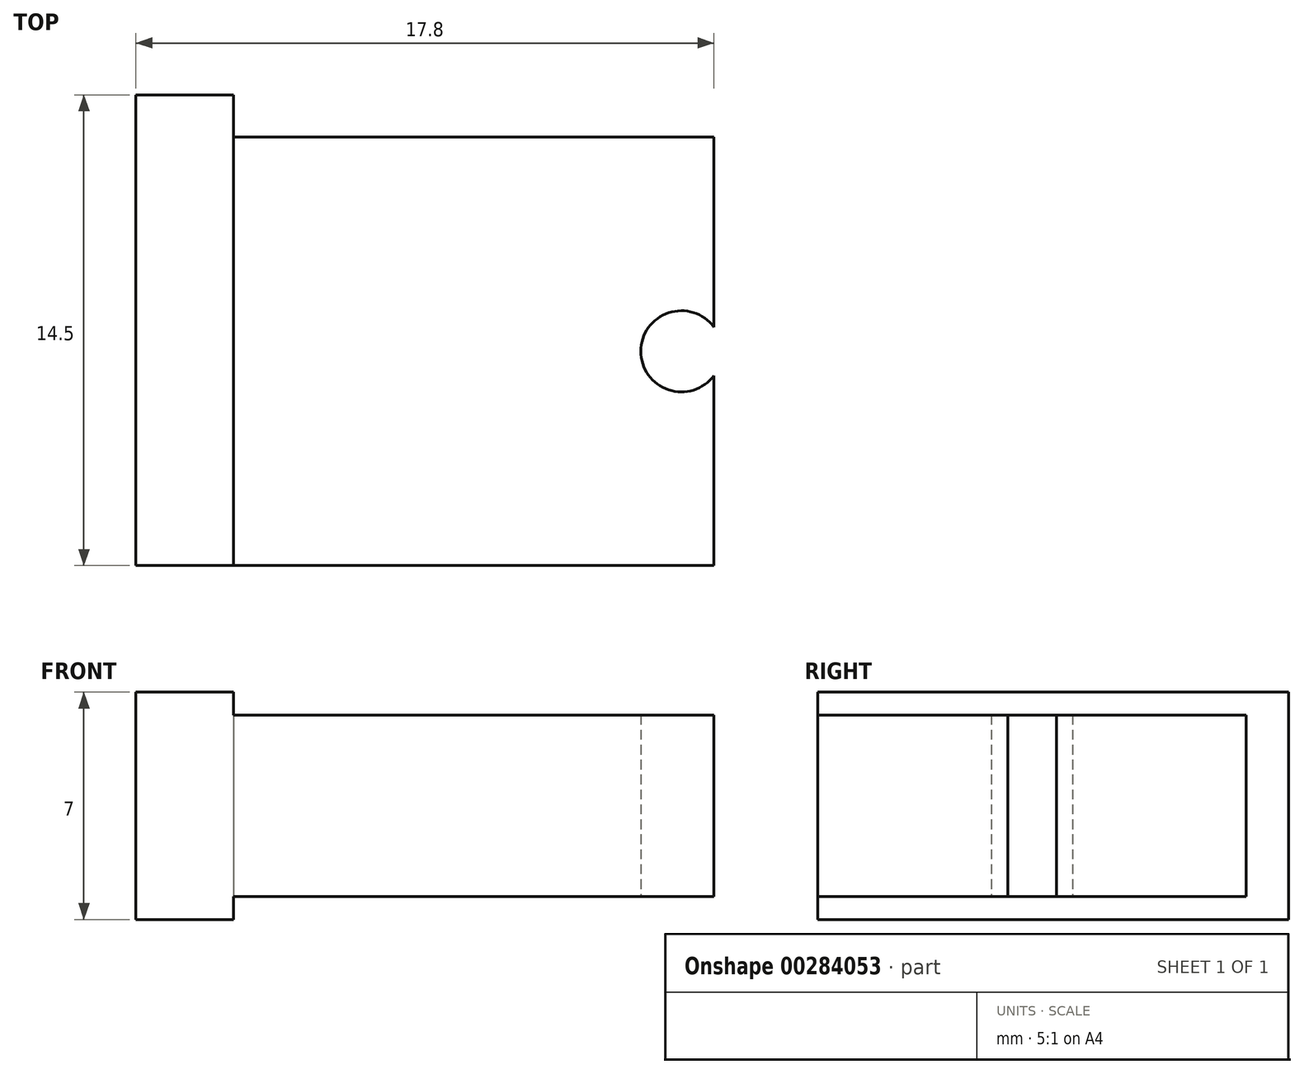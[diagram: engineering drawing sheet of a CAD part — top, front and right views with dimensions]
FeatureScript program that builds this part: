
annotation { "Feature Type Name" : "Feature", "Feature Type Description" : "" }
export const myFeature = defineFeature(function(context is Context, id is Id, definition is map)
    precondition{}
    {
        {
            var Q0;
            Q0=qCreatedBy(makeId("Top.planeOp"),FACE);
            var sketch = newSketch(context, id + "F0", { "sketchPlane" : qUnion([Q0])});
            skLineSegment(sketch, "E0.bottom", {"start": v(-7.4, 6.6) * mm, "end": v(7.4, 6.6) * mm});
            skLineSegment(sketch, "E0.top", {"start": v(-7.4, -6.6) * mm, "end": v(7.4, -6.6) * mm});
            skLineSegment(sketch, "E0.left", {"start": v(-7.4, 6.6) * mm, "end": v(-7.4, -6.6) * mm});
            skLineSegment(sketch, "E0.right", {"start": v(7.4, 6.6) * mm, "end": v(7.4, -6.6) * mm});
            skPoint(sketch, "E0.middle", {"position": v(0, 0) * mm});
            skLineSegment(sketch, "E1", {"start": v(-7.4, 0) * mm, "end": v(6.4, 0) * mm});
            skPoint(sketch, "E1.endSnap0", {"position": v(-7.4, 0) * mm});
            skCircle(sketch, "E2", {"center": v(6.4, 0) * mm, "radius": 1.1 * mm});
            skSolve(sketch);
        }
        {
            var Q0;
            Q0 = qSketchRegion(id + "F0", true);
            extrude(context, id + "F1", {"entities" : qUnion([Q0]), "depth" : 5.6 * mm});
        }
        {
            var Q0;
            Q0=sQuery(id+"F0.wireOp",VERTEX,"E2.center");
            var Q1;
            Q1=makeQuery(id+"F1.opExtrude","SWEPT_BODY",BODY,{"disambiguationData":[OSD([sQuery(id+"F0.wireOp",EDGE,"E0.bottom"),sQuery(id+"F0.wireOp",EDGE,"E0.top"),sQuery(id+"F0.wireOp",EDGE,"E0.left"),sQuery(id+"F0.wireOp",EDGE,"E0.right"),sQuery(id+"F0.wireOp",EDGE,"E2")])]});
            hole(context, id + "F2", {"style" : HoleStyle.SIMPLE, "endStyle" : HoleEndStyle.BLIND, "oppositeDirection" : true, "holeDiameter" : 2.5 * mm, "holeDepth" : 12 * mm, "tappedDepth" : 12 * mm, "tapClearance" : 3, "startFromSketch" : true, "locations" : qUnion([Q0]), "scope" : qUnion([Q1])});
        }
        {
            var Q0;
            Q0=makeQuery(id+"F1.opExtrude","SWEPT_FACE",FACE,{"disambiguationData":[OSD([sQuery(id+"F0.wireOp",EDGE,"E0.left")])]});
            var sketch = newSketch(context, id + "F3", { "sketchPlane" : qUnion([Q0])});
            skLineSegment(sketch, "E3.bottom", {"start": v(-7.9, 6.3) * mm, "end": v(6.6, 6.3) * mm});
            skLineSegment(sketch, "E3.top", {"start": v(-7.9, -0.7) * mm, "end": v(6.6, -0.7) * mm});
            skLineSegment(sketch, "E3.left", {"start": v(-7.9, 6.3) * mm, "end": v(-7.9, -0.7) * mm});
            skLineSegment(sketch, "E3.right", {"start": v(6.6, 6.3) * mm, "end": v(6.6, -0.7) * mm});
            skPoint(sketch, "E3.middle", {"position": v(0, 2.8) * mm});
            skLineSegment(sketch, "E4", {"start": v(-6.6, 2.8) * mm, "end": v(6.6, 2.8) * mm, "construction": true});
            skSolve(sketch);
        }
        {
            var Q0;
            Q0=makeQuery(id+"F3.imprint","IMPRINT",FACE,{"disambiguationData":[TD([[makeQuery(id+"F3.imprint","IMPRINT",EDGE,{"derivedFrom":sQuery(id+"F3.wireOp",EDGE,"E3.bottom")}),-1.0]])]});
            var Q1;
            {var subQ0=sQuery(id+"F0.wireOp",EDGE,"E0.left");Q1=makeQuery(id+"F3.imprint","IMPRINT",FACE,{"disambiguationData":[TD([[makeQuery(id+"F3.imprint","IMPRINT",EDGE,{"derivedFrom":makeQuery(id+"F1.opExtrude","CAP_EDGE",EDGE,{"disambiguationData":[OSD([subQ0])],"isStart":true})}),1.0]])]});}
            extrude(context, id + "F4", {"entities" : qUnion([Q0, Q1]), "operationType" : NewBodyOperationType.ADD, "depth" : 3 * mm});
        }
    });
